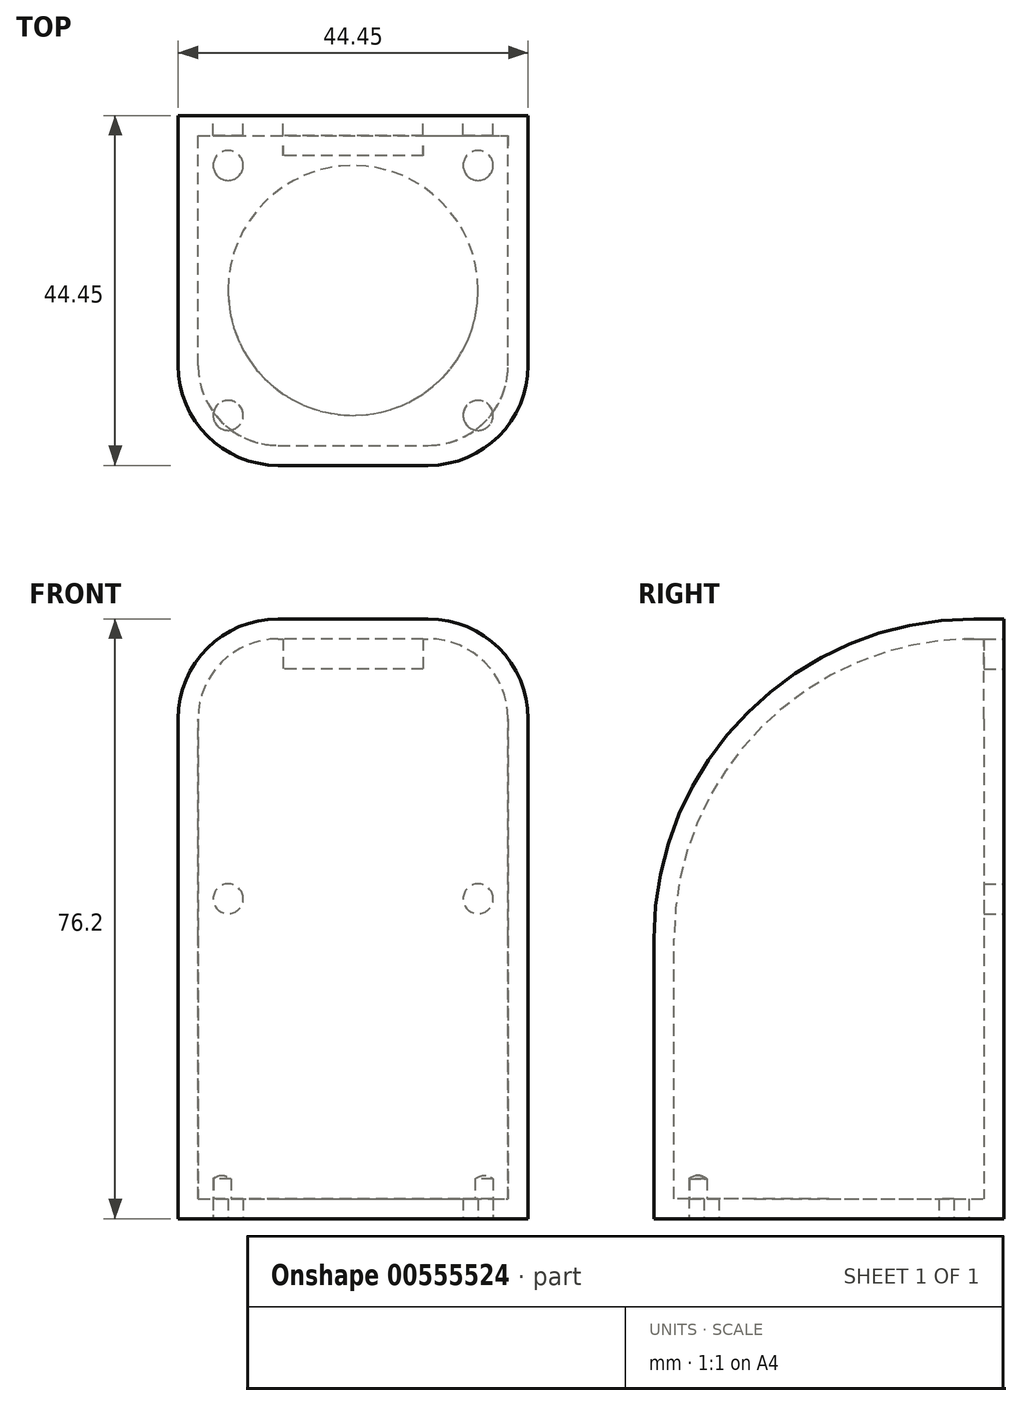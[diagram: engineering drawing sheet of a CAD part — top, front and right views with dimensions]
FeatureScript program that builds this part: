
annotation { "Feature Type Name" : "Feature", "Feature Type Description" : "" }
export const myFeature = defineFeature(function(context is Context, id is Id, definition is map)
    precondition{}
    {
        {
            var Q0;
            Q0=qCreatedBy(makeId("Top.planeOp"),FACE);
            var sketch = newSketch(context, id + "F0", { "sketchPlane" : qUnion([Q0])});
            skLineSegment(sketch, "E0.bottom", {"start": v(-19.28, -19.2) * mm, "end": v(25.17, -19.2) * mm});
            skLineSegment(sketch, "E0.top", {"start": v(-19.28, 25.26) * mm, "end": v(25.17, 25.26) * mm});
            skLineSegment(sketch, "E0.left", {"start": v(-19.28, -19.2) * mm, "end": v(-19.28, 25.26) * mm});
            skLineSegment(sketch, "E0.right", {"start": v(25.17, -19.2) * mm, "end": v(25.17, 25.26) * mm});
            skSolve(sketch);
        }
        {
            var Q0;
            Q0=makeQuery(id+"F0.imprint","IMPRINT",FACE,{"disambiguationData":[TD([[makeQuery(id+"F0.imprint","IMPRINT",EDGE,{"derivedFrom":sQuery(id+"F0.wireOp",EDGE,"E0.bottom")}),1.0]])]});
            extrude(context, id + "F1", {"entities" : qUnion([Q0]), "depth" : 76.2 * mm, "offsetDistance" : 25.4 * mm});
        }
        {
            var Q0;
            Q0=makeQuery(id+"F1.opExtrude","CAP_EDGE",EDGE,{"disambiguationData":[OSD([sQuery(id+"F0.wireOp",EDGE,"E0.bottom")])],"isStart":false});
            fillet(context, id + "F2", {"entities" : qUnion([Q0]), "radius" : 40.64 * mm, "tangentPropagation" : true, "allowEdgeOverflow" : false});
        }
        {
            var Q0;
            Q0=makeQuery(id+"F1.opExtrude","SWEPT_FACE",FACE,{"disambiguationData":[OSD([sQuery(id+"F0.wireOp",EDGE,"E0.top")])]});
            var sketch = newSketch(context, id + "F3", { "sketchPlane" : qUnion([Q0])});
            skLineSegment(sketch, "E1.bottom", {"start": v(-11.84, 73.66) * mm, "end": v(5.94, 73.66) * mm});
            skLineSegment(sketch, "E1.top", {"start": v(-11.84, 69.85) * mm, "end": v(5.94, 69.85) * mm});
            skLineSegment(sketch, "E1.left", {"start": v(-11.84, 73.66) * mm, "end": v(-11.84, 69.85) * mm});
            skLineSegment(sketch, "E1.right", {"start": v(5.94, 73.66) * mm, "end": v(5.94, 69.85) * mm});
            skPoint(sketch, "E2", {"position": v(-18.82, 40.64) * mm});
            skPoint(sketch, "E3", {"position": v(12.93, 40.64) * mm});
            skSolve(sketch);
        }
        {
            var Q0;
            Q0=makeQuery(id+"F2.opFillet","BLEND_EDGE",EDGE,{"blendedFrom":[makeQuery(id+"F1.opExtrude","CAP_EDGE",EDGE,{"disambiguationData":[OSD([sQuery(id+"F0.wireOp",EDGE,"E0.bottom")])],"isStart":false}),makeQuery(id+"F1.opExtrude","SWEPT_FACE",FACE,{"disambiguationData":[OSD([sQuery(id+"F0.wireOp",EDGE,"E0.right")])]})],"blendedInto":[makeQuery(id+"F1.opExtrude","SWEPT_FACE",FACE,{"disambiguationData":[OSD([sQuery(id+"F0.wireOp",EDGE,"E0.right")])]})]});
            var Q1;
            Q1=makeQuery(id+"F2.opFillet","BLEND_EDGE",EDGE,{"blendedFrom":[makeQuery(id+"F1.opExtrude","CAP_EDGE",EDGE,{"disambiguationData":[OSD([sQuery(id+"F0.wireOp",EDGE,"E0.bottom")])],"isStart":false}),makeQuery(id+"F1.opExtrude","SWEPT_FACE",FACE,{"disambiguationData":[OSD([sQuery(id+"F0.wireOp",EDGE,"E0.left")])]})],"blendedInto":[makeQuery(id+"F1.opExtrude","SWEPT_FACE",FACE,{"disambiguationData":[OSD([sQuery(id+"F0.wireOp",EDGE,"E0.left")])]})]});
            fillet(context, id + "F4", {"entities" : qUnion([Q0, Q1]), "radius" : 12.7 * mm, "tangentPropagation" : true, "allowEdgeOverflow" : false});
        }
        {
            var Q0;
            Q0=makeQuery(id+"F1.opExtrude","CAP_FACE",FACE,{"disambiguationData":[OSD([sQuery(id+"F0.wireOp",EDGE,"E0.bottom"),sQuery(id+"F0.wireOp",EDGE,"E0.top"),sQuery(id+"F0.wireOp",EDGE,"E0.left"),sQuery(id+"F0.wireOp",EDGE,"E0.right")])],"isStart":true});
            var sketch = newSketch(context, id + "F5", { "sketchPlane" : qUnion([Q0])});
            skLineSegment(sketch, "E4.bottom", {"start": v(-12.93, 12.84) * mm, "end": v(18.82, 12.84) * mm});
            skLineSegment(sketch, "E4.top", {"start": v(-12.93, -18.9) * mm, "end": v(18.82, -18.9) * mm});
            skLineSegment(sketch, "E4.left", {"start": v(-12.93, 12.84) * mm, "end": v(-12.93, -18.9) * mm});
            skLineSegment(sketch, "E4.right", {"start": v(18.82, 12.84) * mm, "end": v(18.82, -18.9) * mm});
            skPoint(sketch, "E5", {"position": v(2.95, -3.03) * mm});
            skPoint(sketch, "E5.positionSnap0", {"position": v(2.95, 12.84) * mm});
            skSolve(sketch);
        }
        {
            var Q0;
            Q0=makeQuery(id+"F1.opExtrude","SWEPT_FACE",FACE,{"disambiguationData":[OSD([sQuery(id+"F0.wireOp",EDGE,"E0.top")])]});
            var Q1;
            Q1=makeQuery(id+"F1.opExtrude","SWEPT_BODY",BODY,{"disambiguationData":[OSD([sQuery(id+"F0.wireOp",EDGE,"E0.bottom"),sQuery(id+"F0.wireOp",EDGE,"E0.top"),sQuery(id+"F0.wireOp",EDGE,"E0.left"),sQuery(id+"F0.wireOp",EDGE,"E0.right")])]});
            shell(context, id + "F6", {"isHollow" : true, "entities" : qUnion([Q0]), "parts" : qUnion([Q1]), "thickness" : 2.54 * mm});
        }
        {
            var Q0;
            Q0=makeQuery(id+"F3.imprint","IMPRINT",FACE,{"disambiguationData":[TD([[makeQuery(id+"F3.imprint","IMPRINT",EDGE,{"derivedFrom":sQuery(id+"F3.wireOp",EDGE,"E1.bottom")}),-1.0]])]});
            extrude(context, id + "F7", {"entities" : qUnion([Q0]), "operationType" : NewBodyOperationType.REMOVE, "oppositeDirection" : true, "depth" : 5.08 * mm, "offsetDistance" : 25.4 * mm});
        }
        {
            var Q0;
            Q0=sQuery(id+"F5.wireOp",VERTEX,"E4.right.start");
            var Q1;
            Q1=sQuery(id+"F5.wireOp",VERTEX,"E4.bottom.start");
            var Q2;
            Q2=sQuery(id+"F5.wireOp",VERTEX,"E4.right.end");
            var Q3;
            Q3=sQuery(id+"F5.wireOp",VERTEX,"E4.left.end");
            var Q4;
            Q4=makeQuery(id+"F1.opExtrude","SWEPT_BODY",BODY,{"disambiguationData":[OSD([sQuery(id+"F0.wireOp",EDGE,"E0.bottom"),sQuery(id+"F0.wireOp",EDGE,"E0.top"),sQuery(id+"F0.wireOp",EDGE,"E0.left"),sQuery(id+"F0.wireOp",EDGE,"E0.right")])]});
            hole(context, id + "F8", {"style" : HoleStyle.SIMPLE, "endStyle" : HoleEndStyle.BLIND, "holeDiameter" : 3.8 * mm, "holeDepth" : 5.08 * mm, "isTappedThrough" : true, "tappedDepth" : 12.7 * mm, "tapClearance" : 3, "locations" : qUnion([Q0, Q1, Q2, Q3]), "scope" : qUnion([Q4])});
        }
        {
            var Q0;
            Q0=sQuery(id+"F3.wireOp",VERTEX,"E2");
            var Q1;
            Q1=sQuery(id+"F3.wireOp",VERTEX,"E3");
            var Q2;
            Q2=makeQuery(id+"F1.opExtrude","SWEPT_BODY",BODY,{"disambiguationData":[OSD([sQuery(id+"F0.wireOp",EDGE,"E0.bottom"),sQuery(id+"F0.wireOp",EDGE,"E0.top"),sQuery(id+"F0.wireOp",EDGE,"E0.left"),sQuery(id+"F0.wireOp",EDGE,"E0.right")])]});
            hole(context, id + "F9", {"style" : HoleStyle.SIMPLE, "endStyle" : HoleEndStyle.BLIND, "holeDiameter" : 3.8 * mm, "holeDepth" : 5.08 * mm, "isTappedThrough" : true, "tappedDepth" : 12.7 * mm, "tapClearance" : 3, "locations" : qUnion([Q0, Q1]), "scope" : qUnion([Q2])});
        }
        {
            var Q0;
            Q0=sQuery(id+"F5.wireOp",VERTEX,"E5");
            var Q1;
            Q1=makeQuery(id+"F1.opExtrude","SWEPT_BODY",BODY,{"disambiguationData":[OSD([sQuery(id+"F0.wireOp",EDGE,"E0.bottom"),sQuery(id+"F0.wireOp",EDGE,"E0.top"),sQuery(id+"F0.wireOp",EDGE,"E0.left"),sQuery(id+"F0.wireOp",EDGE,"E0.right")])]});
            hole(context, id + "F10", {"style" : HoleStyle.SIMPLE, "endStyle" : HoleEndStyle.BLIND, "holeDiameter" : 31.75 * mm, "holeDepth" : 5.08 * mm, "isTappedThrough" : true, "tappedDepth" : 12.7 * mm, "tapClearance" : 3, "locations" : qUnion([Q0]), "scope" : qUnion([Q1])});
        }
    });
